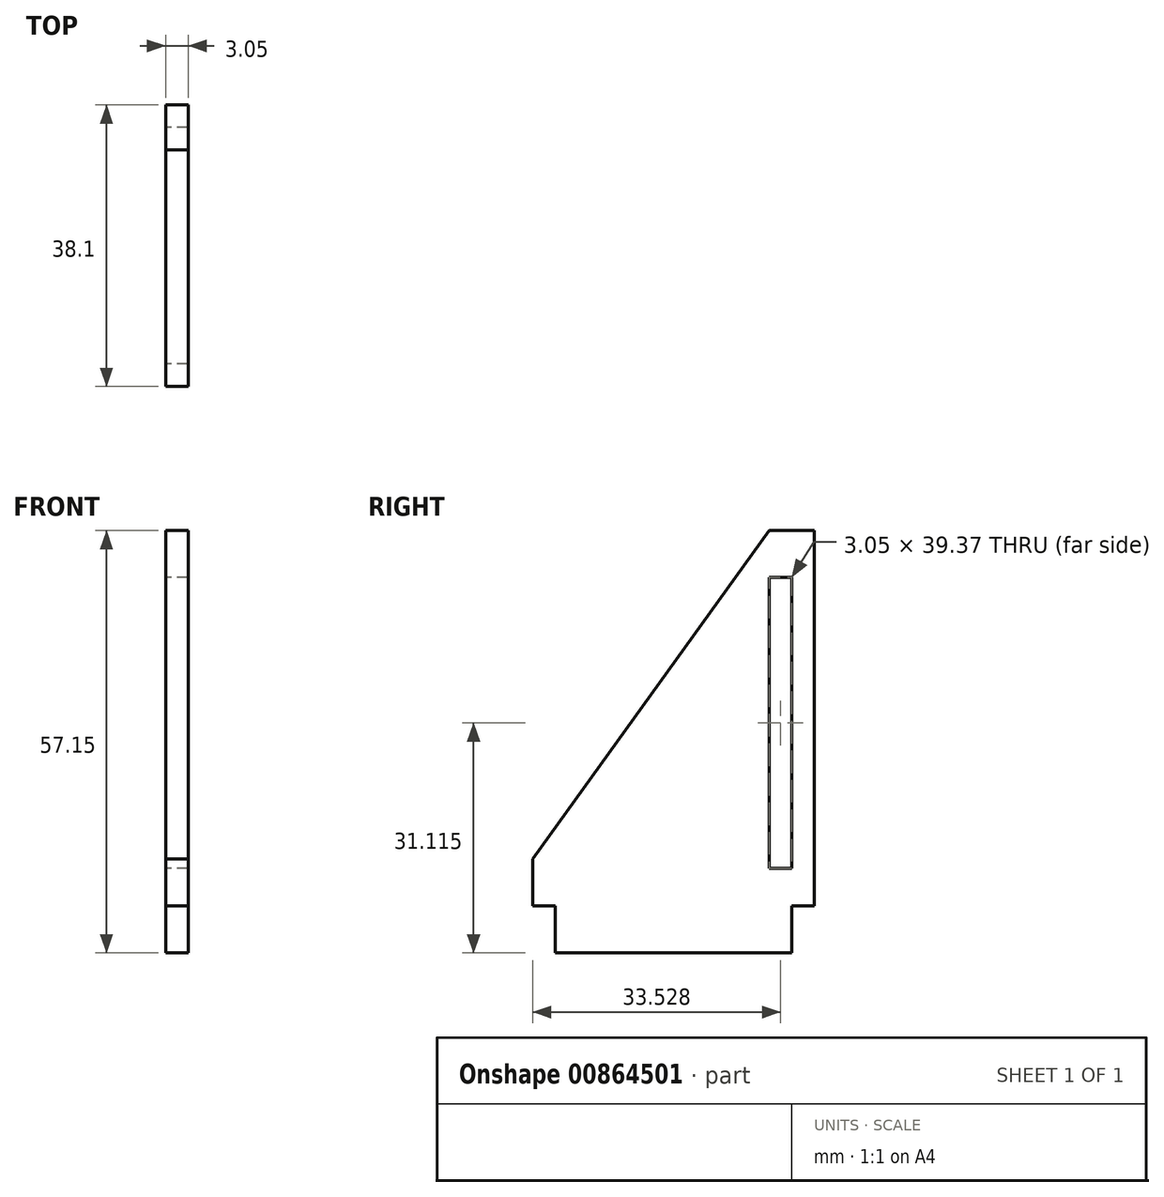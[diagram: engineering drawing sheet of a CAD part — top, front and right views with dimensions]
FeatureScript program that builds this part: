
annotation { "Feature Type Name" : "Feature", "Feature Type Description" : "" }
export const myFeature = defineFeature(function(context is Context, id is Id, definition is map)
    precondition{}
    {
        {
            var Q0;
            Q0=qCreatedBy(makeId("Right.planeOp"),FACE);
            var sketch = newSketch(context, id + "F0", { "sketchPlane" : qUnion([Q0])});
            skLineSegment(sketch, "E0", {"start": v(0, 50.8) * mm, "end": v(0, 0) * mm});
            skLineSegment(sketch, "E1", {"start": v(0, 0) * mm, "end": v(-3.05, 0) * mm});
            skLineSegment(sketch, "E2", {"start": v(-3.05, 0) * mm, "end": v(-3.05, -6.35) * mm});
            skLineSegment(sketch, "E3", {"start": v(-3.05, -6.35) * mm, "end": v(-35.05, -6.35) * mm});
            skLineSegment(sketch, "E4", {"start": v(-35.05, -6.35) * mm, "end": v(-35.05, 0) * mm});
            skLineSegment(sketch, "E5", {"start": v(-35.05, 0) * mm, "end": v(-38.1, 0) * mm});
            skLineSegment(sketch, "E6", {"start": v(-38.1, 0) * mm, "end": v(-38.1, 6.35) * mm});
            skLineSegment(sketch, "E7.bottom", {"start": v(-6.1, 44.45) * mm, "end": v(-3.05, 44.45) * mm});
            skLineSegment(sketch, "E7.top", {"start": v(-6.1, 5.08) * mm, "end": v(-3.05, 5.08) * mm});
            skLineSegment(sketch, "E7.left", {"start": v(-6.1, 44.45) * mm, "end": v(-6.1, 5.08) * mm});
            skLineSegment(sketch, "E7.right", {"start": v(-3.05, 44.45) * mm, "end": v(-3.05, 5.08) * mm});
            skLineSegment(sketch, "E8", {"start": v(0, 50.8) * mm, "end": v(-6.1, 50.8) * mm});
            skLineSegment(sketch, "E9", {"start": v(-6.1, 50.8) * mm, "end": v(-38.1, 6.35) * mm});
            skSolve(sketch);
        }
        {
            var Q0;
            Q0 = qSketchRegion(id + "F0", true);
            extrude(context, id + "F1", {"entities" : qUnion([Q0]), "depth" : 3.05 * mm, "offsetDistance" : 25.4 * mm});
        }
    });
